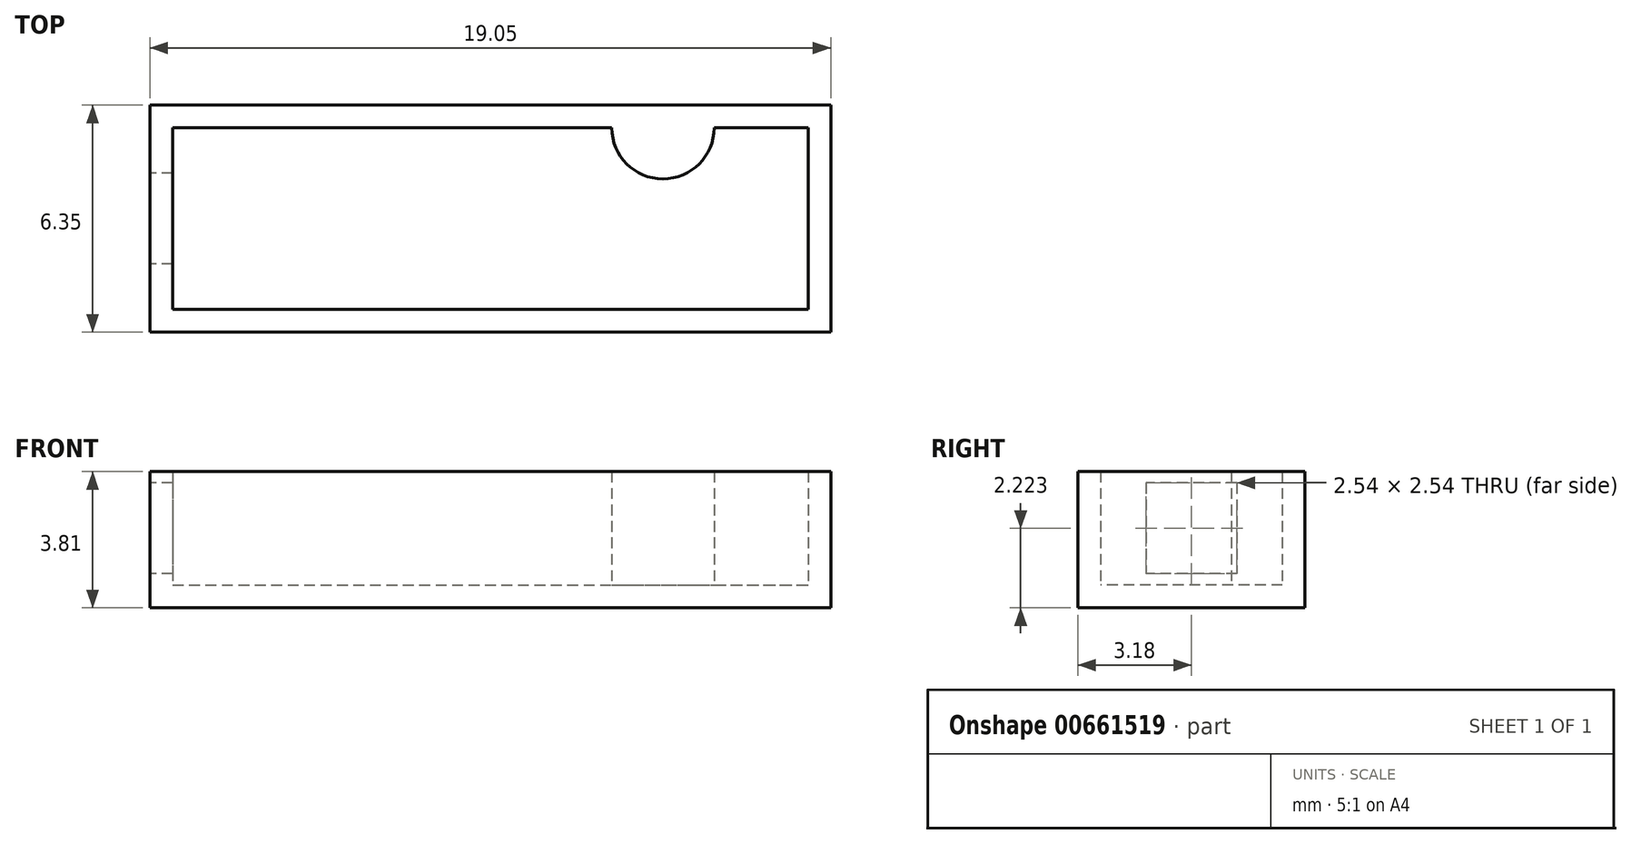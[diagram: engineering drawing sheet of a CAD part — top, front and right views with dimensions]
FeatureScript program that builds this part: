
annotation { "Feature Type Name" : "Feature", "Feature Type Description" : "" }
export const myFeature = defineFeature(function(context is Context, id is Id, definition is map)
    precondition{}
    {
        {
            var Q0;
            Q0=qCreatedBy(makeId("Top.planeOp"),FACE);
            var sketch = newSketch(context, id + "F0", { "sketchPlane" : qUnion([Q0])});
            skLineSegment(sketch, "E0.bottom", {"start": v(10.05, 35.75) * mm, "end": v(29.1, 35.75) * mm});
            skLineSegment(sketch, "E0.top", {"start": v(10.05, 29.4) * mm, "end": v(29.1, 29.4) * mm});
            skLineSegment(sketch, "E0.left", {"start": v(10.05, 35.75) * mm, "end": v(10.05, 29.4) * mm});
            skLineSegment(sketch, "E0.right", {"start": v(29.1, 35.75) * mm, "end": v(29.1, 29.4) * mm});
            skSolve(sketch);
        }
        {
            var Q0;
            Q0=makeQuery(id+"F0.imprint","IMPRINT",FACE,{"disambiguationData":[TD([[makeQuery(id+"F0.imprint","IMPRINT",EDGE,{"derivedFrom":sQuery(id+"F0.wireOp",EDGE,"E0.bottom")}),-1.0]])]});
            extrude(context, id + "F1", {"entities" : qUnion([Q0]), "depth" : 3.8 * mm, "offsetDistance" : 25.4 * mm});
        }
        {
            var Q0;
            Q0=makeQuery(id+"F1.opExtrude","CAP_FACE",FACE,{"disambiguationData":[OSD([sQuery(id+"F0.wireOp",EDGE,"E0.bottom"),sQuery(id+"F0.wireOp",EDGE,"E0.top"),sQuery(id+"F0.wireOp",EDGE,"E0.left"),sQuery(id+"F0.wireOp",EDGE,"E0.right")])],"isStart":false});
            shell(context, id + "F2", {"entities" : qUnion([Q0]), "thickness" : 0.64 * mm});
        }
        {
            var Q0;
            Q0=makeQuery(id+"F2.opShell","OFFSET_FACE",FACE,{"disambiguationData":[OSD([sQuery(id+"F0.wireOp",EDGE,"E0.bottom"),sQuery(id+"F0.wireOp",EDGE,"E0.top"),sQuery(id+"F0.wireOp",EDGE,"E0.left"),sQuery(id+"F0.wireOp",EDGE,"E0.right")])]});
            var sketch = newSketch(context, id + "F3", { "sketchPlane" : qUnion([Q0])});
            skCircle(sketch, "E1", {"center": v(24.4, 35.12) * mm, "radius": 1.43 * mm});
            skSolve(sketch);
        }
        {
            var Q0;
            {var subQ0=sQuery(id+"F3.wireOp",EDGE,"E1");var subQ1=sQuery(id+"F0.wireOp",EDGE,"E0.bottom");var subQ2=makeQuery(id+"F2.opShell","OFFSET_EDGE",EDGE,{"disambiguationData":[OSD([subQ1]),TDD([makeQuery(id+"F1.opExtrude","CAP_EDGE",EDGE,{"disambiguationData":[OSD([subQ1])],"isStart":true})])]});var subQ3=makeQuery(id+"F3.imprint","INTERSECT",VERTEX,{"disambiguationData":[OD(0.0)],"derivedFrom":[subQ2,subQ0]});Q0=makeQuery(id+"F3.imprint","IMPRINT",FACE,{"disambiguationData":[TD([[makeQuery(id+"F3.imprint","IMPRINT",EDGE,{"disambiguationData":[TD([[subQ3,-1.0]])],"derivedFrom":subQ0}),1.0]])]});}
            extrude(context, id + "F4", {"entities" : qUnion([Q0]), "operationType" : NewBodyOperationType.ADD, "depth" : 3.17 * mm, "offsetDistance" : 25.4 * mm});
        }
        {
            var Q0;
            Q0=makeQuery(id+"F1.opExtrude","SWEPT_FACE",FACE,{"disambiguationData":[OSD([sQuery(id+"F0.wireOp",EDGE,"E0.left")])]});
            var sketch = newSketch(context, id + "F5", { "sketchPlane" : qUnion([Q0])});
            skLineSegment(sketch, "E2", {"start": v(-35.75, 0.63) * mm, "end": v(-29.4, 0.64) * mm});
            skLineSegment(sketch, "E3.bottom", {"start": v(-33.85, 3.5) * mm, "end": v(-31.3, 3.5) * mm});
            skLineSegment(sketch, "E3.top", {"start": v(-33.85, 0.95) * mm, "end": v(-31.3, 0.95) * mm});
            skLineSegment(sketch, "E3.left", {"start": v(-33.85, 3.5) * mm, "end": v(-33.85, 0.95) * mm});
            skLineSegment(sketch, "E3.right", {"start": v(-31.3, 3.5) * mm, "end": v(-31.3, 0.95) * mm});
            skLineSegment(sketch, "E4", {"start": v(-29.4, 3.81) * mm, "end": v(-29.4, 0.64) * mm});
            skLineSegment(sketch, "E5", {"start": v(-29.4, 2.22) * mm, "end": v(-35.75, 2.22) * mm});
            skLineSegment(sketch, "E6", {"start": v(-32.58, 3.81) * mm, "end": v(-32.58, 0.64) * mm});
            skSolve(sketch);
        }
        {
            var Q0;
            {var subQ0=sQuery(id+"F5.wireOp",EDGE,"E3.left");var subQ1=sQuery(id+"F5.wireOp",EDGE,"E3.bottom");var subQ2=makeQuery(id+"F5.imprint","INTERSECT",VERTEX,{"derivedFrom":[subQ1,subQ0]});Q0=makeQuery(id+"F5.imprint","IMPRINT",FACE,{"disambiguationData":[TD([[makeQuery(id+"F5.imprint","IMPRINT",EDGE,{"disambiguationData":[TD([[subQ2,-1.0]])],"derivedFrom":subQ1}),-1.0]])]});}
            var Q1;
            {var subQ0=sQuery(id+"F5.wireOp",EDGE,"E3.right");var subQ1=sQuery(id+"F5.wireOp",EDGE,"E3.bottom");var subQ2=makeQuery(id+"F5.imprint","INTERSECT",VERTEX,{"derivedFrom":[subQ1,subQ0]});Q1=makeQuery(id+"F5.imprint","IMPRINT",FACE,{"disambiguationData":[TD([[makeQuery(id+"F5.imprint","IMPRINT",EDGE,{"disambiguationData":[TD([[subQ2,1.0]])],"derivedFrom":subQ1}),-1.0]])]});}
            var Q2;
            {var subQ0=sQuery(id+"F5.wireOp",EDGE,"E3.right");var subQ1=sQuery(id+"F5.wireOp",EDGE,"E3.top");var subQ2=makeQuery(id+"F5.imprint","INTERSECT",VERTEX,{"derivedFrom":[subQ1,subQ0]});Q2=makeQuery(id+"F5.imprint","IMPRINT",FACE,{"disambiguationData":[TD([[makeQuery(id+"F5.imprint","IMPRINT",EDGE,{"disambiguationData":[TD([[subQ2,1.0]])],"derivedFrom":subQ1}),1.0]])]});}
            var Q3;
            {var subQ0=sQuery(id+"F5.wireOp",EDGE,"E3.left");var subQ1=sQuery(id+"F5.wireOp",EDGE,"E3.top");var subQ2=makeQuery(id+"F5.imprint","INTERSECT",VERTEX,{"derivedFrom":[subQ1,subQ0]});Q3=makeQuery(id+"F5.imprint","IMPRINT",FACE,{"disambiguationData":[TD([[makeQuery(id+"F5.imprint","IMPRINT",EDGE,{"disambiguationData":[TD([[subQ2,-1.0]])],"derivedFrom":subQ1}),1.0]])]});}
            extrude(context, id + "F6", {"entities" : qUnion([Q0, Q1, Q2, Q3]), "operationType" : NewBodyOperationType.REMOVE, "oppositeDirection" : true, "depth" : 0.64 * mm, "offsetDistance" : 25.4 * mm});
        }
    });
